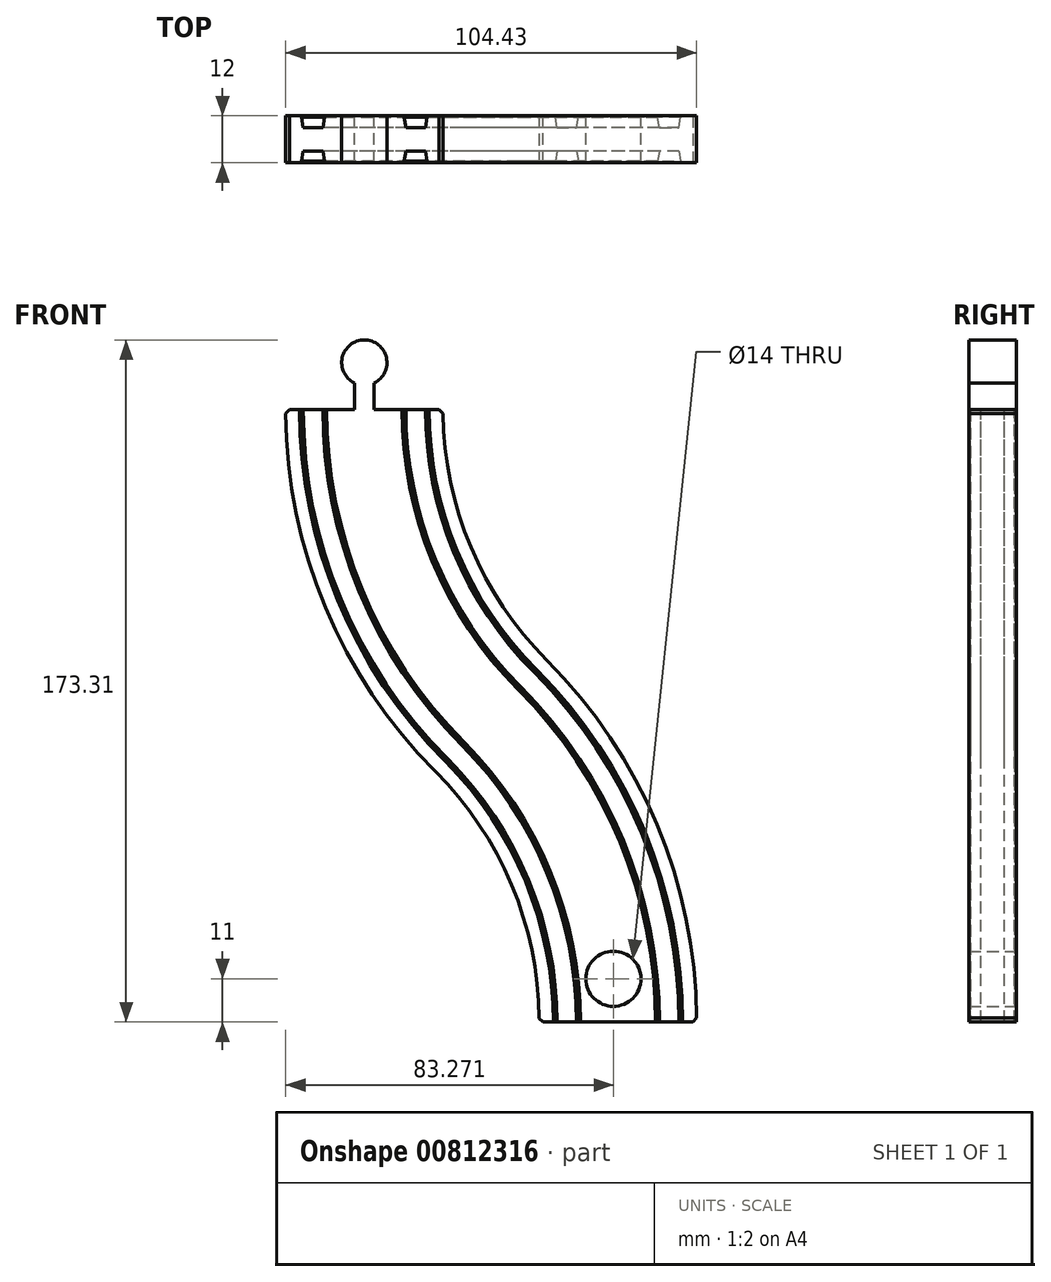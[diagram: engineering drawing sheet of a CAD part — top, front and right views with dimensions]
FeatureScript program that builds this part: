
annotation { "Feature Type Name" : "Feature", "Feature Type Description" : "" }
export const myFeature = defineFeature(function(context is Context, id is Id, definition is map)
    precondition{}
    {
        {
            var Q0;
            Q0=qCreatedBy(makeId("Top.planeOp"),FACE);
            var sketch = newSketch(context, id + "F0", { "sketchPlane" : qUnion([Q0])});
            skLineSegment(sketch, "E0.bottom", {"start": v(-20, 6) * mm, "end": v(20, 6) * mm});
            skLineSegment(sketch, "E0.top", {"start": v(-20, -6) * mm, "end": v(20, -6) * mm});
            skLineSegment(sketch, "E0.left", {"start": v(-20, 6) * mm, "end": v(-20, -6) * mm});
            skLineSegment(sketch, "E0.right", {"start": v(20, 6) * mm, "end": v(20, -6) * mm});
            skLineSegment(sketch, "E1", {"start": v(10.53, 3) * mm, "end": v(15.53, 3) * mm});
            skLineSegment(sketch, "E2", {"start": v(-15.53, 3) * mm, "end": v(-10.53, 3) * mm});
            skLineSegment(sketch, "E3", {"start": v(-20, 6) * mm, "end": v(20, -6) * mm, "construction": true});
            skLineSegment(sketch, "E4", {"start": v(-10.53, 3) * mm, "end": v(-10, 6) * mm});
            skLineSegment(sketch, "E5", {"start": v(-15.53, 3) * mm, "end": v(-16, 6) * mm});
            skLineSegment(sketch, "E6", {"start": v(10.53, 3) * mm, "end": v(10, 6) * mm});
            skLineSegment(sketch, "E7", {"start": v(15.53, 3) * mm, "end": v(16, 6) * mm});
            skLineSegment(sketch, "E8", {"start": v(15.53, -3) * mm, "end": v(10.53, -3) * mm});
            skLineSegment(sketch, "E9", {"start": v(15.53, -3) * mm, "end": v(16, -6) * mm});
            skLineSegment(sketch, "E10", {"start": v(10.53, -3) * mm, "end": v(10, -6) * mm});
            skLineSegment(sketch, "E11", {"start": v(-10.53, -3) * mm, "end": v(-15.53, -3) * mm});
            skLineSegment(sketch, "E12", {"start": v(-10.53, -3) * mm, "end": v(-10, -6) * mm});
            skLineSegment(sketch, "E13", {"start": v(-15.53, -3) * mm, "end": v(-16, -6) * mm});
            skLineSegment(sketch, "E14", {"start": v(10, 6) * mm, "end": v(10, -6) * mm, "construction": true});
            skLineSegment(sketch, "E15", {"start": v(16, 6) * mm, "end": v(16, -6) * mm, "construction": true});
            skLineSegment(sketch, "E16", {"start": v(10.53, 3) * mm, "end": v(10.53, -6) * mm, "construction": true});
            skLineSegment(sketch, "E17", {"start": v(-15.53, 3) * mm, "end": v(-15.53, -6) * mm, "construction": true});
            skSolve(sketch);
        }
        {
            var Q0;
            Q0=qCreatedBy(makeId("Front.planeOp"),FACE);
            var sketch = newSketch(context, id + "F1", { "sketchPlane" : qUnion([Q0])});
            skArc(sketch, "E18", {"start": v(0, 0) * mm, "mid": v(-8.37, 42.1) * mm, "end": v(-32.22, 77.78) * mm});
            skLineSegment(sketch, "E19", {"start": v(-110, 0) * mm, "end": v(45.56, 155.56) * mm, "construction": true});
            skArc(sketch, "E20", {"start": v(-32.22, 77.78) * mm, "mid": v(-56.06, 113.47) * mm, "end": v(-64.44, 155.56) * mm});
            skSolve(sketch);
        }
        {
            var Q0;
            Q0=makeQuery(id+"F0.imprint","IMPRINT",FACE,{"disambiguationData":[TD([[makeQuery(id+"F0.imprint","IMPRINT",EDGE,{"derivedFrom":sQuery(id+"F0.wireOp",EDGE,"E0.top")}),1.0]])]});
            var Q1;
            Q1=sQuery(id+"F1.wireOp",EDGE,"E18");
            var Q2;
            Q2=sQuery(id+"F1.wireOp",EDGE,"E20");
            sweep(context, id + "F2", {"profiles" : qUnion([Q0]), "path" : qUnion([Q1, Q2])});
        }
        {
            var Q0;
            Q0=makeQuery(id+"F2.opSweep","SWEPT_EDGE",EDGE,{"disambiguationData":[OSD([sQuery(id+"F0.wireOp",EDGE,"E0.bottom"),sQuery(id+"F0.wireOp",EDGE,"E4"),sQuery(id+"F1.wireOp",EDGE,"QheDVgyy-v1Xf-DTUT-CkoZ-R19I37jAeaWV")])]});
            var Q1;
            Q1=makeQuery(id+"F2.opSweep","SWEPT_EDGE",EDGE,{"disambiguationData":[OSD([sQuery(id+"F0.wireOp",EDGE,"E0.bottom"),sQuery(id+"F0.wireOp",EDGE,"E5"),sQuery(id+"F1.wireOp",EDGE,"QheDVgyy-v1Xf-DTUT-CkoZ-R19I37jAeaWV")])]});
            var Q2;
            Q2=makeQuery(id+"F2.opSweep","SWEPT_EDGE",EDGE,{"disambiguationData":[OSD([sQuery(id+"F0.wireOp",EDGE,"E0.bottom"),sQuery(id+"F0.wireOp",EDGE,"E6"),sQuery(id+"F1.wireOp",EDGE,"QheDVgyy-v1Xf-DTUT-CkoZ-R19I37jAeaWV")])]});
            var Q3;
            Q3=makeQuery(id+"F2.opSweep","SWEPT_EDGE",EDGE,{"disambiguationData":[OSD([sQuery(id+"F0.wireOp",EDGE,"E0.bottom"),sQuery(id+"F0.wireOp",EDGE,"E7"),sQuery(id+"F1.wireOp",EDGE,"QheDVgyy-v1Xf-DTUT-CkoZ-R19I37jAeaWV")])]});
            var Q4;
            Q4=makeQuery(id+"F2.opSweep","SWEPT_EDGE",EDGE,{"disambiguationData":[OSD([sQuery(id+"F0.wireOp",EDGE,"E0.top"),sQuery(id+"F0.wireOp",EDGE,"E10"),sQuery(id+"F1.wireOp",EDGE,"E18")])]});
            var Q5;
            Q5=makeQuery(id+"F2.opSweep","SWEPT_EDGE",EDGE,{"disambiguationData":[OSD([sQuery(id+"F0.wireOp",EDGE,"E0.top"),sQuery(id+"F0.wireOp",EDGE,"E9"),sQuery(id+"F1.wireOp",EDGE,"E18")])]});
            var Q6;
            Q6=makeQuery(id+"F2.opSweep","SWEPT_EDGE",EDGE,{"disambiguationData":[OSD([sQuery(id+"F0.wireOp",EDGE,"E0.top"),sQuery(id+"F0.wireOp",EDGE,"E13"),sQuery(id+"F1.wireOp",EDGE,"E18")])]});
            var Q7;
            Q7=makeQuery(id+"F2.opSweep","SWEPT_EDGE",EDGE,{"disambiguationData":[OSD([sQuery(id+"F0.wireOp",EDGE,"E0.top"),sQuery(id+"F0.wireOp",EDGE,"E12"),sQuery(id+"F1.wireOp",EDGE,"E18")])]});
            chamfer(context, id + "F3", {"entities" : qUnion([Q0, Q1, Q2, Q3, Q4, Q5, Q6, Q7]), "width" : 0.5 * mm, "tangentPropagation" : true});
        }
        {
            var Q0;
            Q0=qCreatedBy(makeId("Front.planeOp"),FACE);
            var sketch = newSketch(context, id + "F4", { "sketchPlane" : qUnion([Q0])});
            skLineSegment(sketch, "E21.0", {"start": v(-47.4, 155.56) * mm, "end": v(-54.94, 155.56) * mm});
            skSolve(sketch);
        }
        {
            var Q0;
            Q0=qCreatedBy(makeId("Front.planeOp"),FACE);
            var sketch = newSketch(context, id + "F5", { "sketchPlane" : qUnion([Q0])});
            skLineSegment(sketch, "E22.0", {"start": v(-9.5, 0) * mm, "end": v(-9.5, 0) * mm});
            skLineSegment(sketch, "E23.bottom", {"start": v(2.34, 0) * mm, "end": v(-4.66, 0) * mm});
            skLineSegment(sketch, "E23.top", {"start": v(2.34, 5) * mm, "end": v(-4.66, 5) * mm});
            skLineSegment(sketch, "E23.left", {"start": v(2.34, 0) * mm, "end": v(2.34, 5) * mm});
            skLineSegment(sketch, "E23.right", {"start": v(-4.66, 0) * mm, "end": v(-4.66, 5) * mm});
            skLineSegment(sketch, "E24", {"start": v(8.34, 0) * mm, "end": v(2.34, 0) * mm, "construction": true});
            skLineSegment(sketch, "E25", {"start": v(-4.66, 0) * mm, "end": v(-10.66, 0) * mm, "construction": true});
            skCircle(sketch, "E26", {"center": v(-1.16, 11) * mm, "radius": 7 * mm});
            skPoint(sketch, "E26.centerSnap0", {"position": v(-1.16, 5) * mm});
            skSolve(sketch);
        }
        {
            var Q0;
            {var subQ0=sQuery(id+"F1.wireOp",EDGE,"QheDVgyy-v1Xf-DTUT-CkoZ-R19I37jAeaWV");var subQ1=sQuery(id+"F0.wireOp",EDGE,"E0.bottom");Q0=makeQuery(id+"F2.opSweep","SWEPT_FACE",FACE,{"disambiguationData":[OSD([subQ1,subQ0]),TDD([makeQuery(id+"F0.imprint","IMPRINT",EDGE,{"disambiguationData":[TD([[makeQuery(id+"F0.imprint","INTERSECT",VERTEX,{"derivedFrom":[subQ1,sQuery(id+"F0.wireOp",EDGE,"E4")]}),-1.0]])],"derivedFrom":subQ1}),subQ0])]});}
            var sketch = newSketch(context, id + "F6", { "sketchPlane" : qUnion([Q0])});
            skCircle(sketch, "E27.0", {"center": v(1.16, 11) * mm, "radius": 7 * mm});
            skLineSegment(sketch, "E28.0", {"start": v(4.66, 0) * mm, "end": v(4.66, 5) * mm});
            skLineSegment(sketch, "E29.0", {"start": v(-2.34, 0) * mm, "end": v(-2.34, 5) * mm});
            skLineSegment(sketch, "E30.0", {"start": v(-2.34, 5) * mm, "end": v(4.66, 5) * mm});
            skLineSegment(sketch, "E31.0", {"start": v(-8.34, 0) * mm, "end": v(10.66, 0) * mm});
            skSolve(sketch);
        }
        {
            var Q0;
            {var subQ5=sQuery(id+"F6.wireOp",EDGE,"E30.0");Q0=makeQuery(id+"F6.imprint","IMPRINT",FACE,{"disambiguationData":[TD([[makeQuery(id+"F6.imprint","IMPRINT",EDGE,{"derivedFrom":subQ5}),1.0]])]});}
            var Q1;
            {var subQ0=sQuery(id+"F6.wireOp",EDGE,"E28.0");var subQ1=sQuery(id+"F6.wireOp",EDGE,"E27.0");var subQ2=makeQuery(id+"F6.imprint","INTERSECT",VERTEX,{"derivedFrom":[subQ1,subQ0]});Q1=makeQuery(id+"F6.imprint","IMPRINT",FACE,{"disambiguationData":[TD([[makeQuery(id+"F6.imprint","IMPRINT",EDGE,{"disambiguationData":[TD([[subQ2,-1.0]])],"derivedFrom":subQ1}),1.0]])]});}
            var Q2;
            {var subQ5=sQuery(id+"F6.wireOp",EDGE,"E30.0");Q2=makeQuery(id+"F6.imprint","IMPRINT",FACE,{"disambiguationData":[TD([[makeQuery(id+"F6.imprint","IMPRINT",EDGE,{"derivedFrom":subQ5}),-1.0]])]});}
            extrude(context, id + "F7", {"entities" : qUnion([Q0, Q1, Q2]), "operationType" : NewBodyOperationType.REMOVE, "oppositeDirection" : true, "depth" : 25.4 * mm, "offsetDistance" : 25.4 * mm});
        }
        {
            var Q0;
            Q0=makeQuery(id+"F2.opSweep","CAP_EDGE",EDGE,{"disambiguationData":[OSD([sQuery(id+"F0.wireOp",EDGE,"E0.right"),sQuery(id+"F1.wireOp",VERTEX,"QheDVgyy-v1Xf-DTUT-CkoZ-R19I37jAeaWV.start")])],"isStart":false});
            var Q1;
            Q1=makeQuery(id+"F2.opSweep","CAP_EDGE",EDGE,{"disambiguationData":[OSD([sQuery(id+"F0.wireOp",EDGE,"E0.left"),sQuery(id+"F1.wireOp",VERTEX,"QheDVgyy-v1Xf-DTUT-CkoZ-R19I37jAeaWV.start")])],"isStart":false});
            var Q2;
            Q2=makeQuery(id+"F2.opSweep","CAP_EDGE",EDGE,{"disambiguationData":[OSD([sQuery(id+"F0.wireOp",EDGE,"E0.left"),sQuery(id+"F1.wireOp",VERTEX,"QheDVgyy-v1Xf-DTUT-CkoZ-R19I37jAeaWV.end")])],"isStart":true});
            var Q3;
            Q3=makeQuery(id+"F2.opSweep","CAP_EDGE",EDGE,{"disambiguationData":[OSD([sQuery(id+"F0.wireOp",EDGE,"E0.right"),sQuery(id+"F1.wireOp",VERTEX,"QheDVgyy-v1Xf-DTUT-CkoZ-R19I37jAeaWV.end")])],"isStart":true});
            chamfer(context, id + "F8", {"entities" : qUnion([Q0, Q1, Q2, Q3]), "width" : 1 * mm, "tangentPropagation" : true});
        }
        {
            var Q0;
            {var subQ0=sQuery(id+"F1.wireOp",EDGE,"E18");var subQ1=sQuery(id+"F0.wireOp",EDGE,"E0.bottom");Q0=makeQuery(id+"F2.opSweep","SWEPT_FACE",FACE,{"disambiguationData":[OSD([subQ1,subQ0]),TDD([makeQuery(id+"F0.imprint","IMPRINT",EDGE,{"disambiguationData":[TD([[makeQuery(id+"F0.imprint","INTERSECT",VERTEX,{"derivedFrom":[subQ1,sQuery(id+"F0.wireOp",EDGE,"E4")]}),-1.0]])],"derivedFrom":subQ1}),subQ0])]});}
            var sketch = newSketch(context, id + "F9", { "sketchPlane" : qUnion([Q0])});
            skLineSegment(sketch, "E32", {"start": v(61.94, 155.56) * mm, "end": v(61.94, 162.56) * mm});
            skLineSegment(sketch, "E33", {"start": v(61.94, 162.56) * mm, "end": v(66.94, 162.56) * mm});
            skLineSegment(sketch, "E34", {"start": v(66.94, 162.56) * mm, "end": v(66.94, 155.56) * mm});
            skLineSegment(sketch, "E35", {"start": v(61.94, 155.56) * mm, "end": v(54.94, 155.56) * mm, "construction": true});
            skLineSegment(sketch, "E36", {"start": v(66.94, 155.56) * mm, "end": v(73.94, 155.56) * mm, "construction": true});
            skLineSegment(sketch, "E37", {"start": v(64.44, 155.56) * mm, "end": v(64.44, 167.56) * mm, "construction": true});
            skCircle(sketch, "E38", {"center": v(64.44, 167.56) * mm, "radius": 5.75 * mm});
            skSolve(sketch);
        }
        {
            var Q0;
            {var subQ0=sQuery(id+"F4.wireOp",EDGE,"y3DwgqY9-x9Yp-s0zT-CjDQ-IHoX7M89SHfb");var subQ1=sQuery(id+"F4.wireOp",EDGE,"XYbCKtlu-qh1t-nVi3-P5wv-khNMWSoX9qSB");var subQ2=makeQuery(id+"F4.imprint","INTERSECT",VERTEX,{"derivedFrom":[subQ1,subQ0]});Q0=makeQuery(id+"F4.imprint","IMPRINT",FACE,{"disambiguationData":[TD([[makeQuery(id+"F4.imprint","IMPRINT",EDGE,{"disambiguationData":[TD([[subQ2,1.0]])],"derivedFrom":subQ1}),-1.0]])]});}
            var Q1;
            {var subQ0=sQuery(id+"F4.wireOp",EDGE,"rqF1hGhq-thtG-Dqzb-XRaq-cd5KwwhKuCuG");var subQ1=sQuery(id+"F4.wireOp",EDGE,"E21.0");var subQ2=makeQuery(id+"F4.imprint","INTERSECT",VERTEX,{"derivedFrom":[subQ1,subQ0]});Q1=makeQuery(id+"F4.imprint","IMPRINT",FACE,{"disambiguationData":[TD([[makeQuery(id+"F4.imprint","IMPRINT",EDGE,{"disambiguationData":[TD([[subQ2,-1.0]])],"derivedFrom":subQ1}),-1.0]])]});}
            var Q2;
            {var subQ0=sQuery(id+"F4.wireOp",EDGE,"y3DwgqY9-x9Yp-s0zT-CjDQ-IHoX7M89SHfb");var subQ1=sQuery(id+"F4.wireOp",EDGE,"E21.0");var subQ2=makeQuery(id+"F4.imprint","INTERSECT",VERTEX,{"derivedFrom":[subQ1,subQ0]});Q2=makeQuery(id+"F4.imprint","IMPRINT",FACE,{"disambiguationData":[TD([[makeQuery(id+"F4.imprint","IMPRINT",EDGE,{"disambiguationData":[TD([[subQ2,1.0]])],"derivedFrom":subQ1}),-1.0]])]});}
            var Q3;
            {var subQ0=sQuery(id+"F4.wireOp",EDGE,"y3DwgqY9-x9Yp-s0zT-CjDQ-IHoX7M89SHfb");var subQ1=sQuery(id+"F4.wireOp",EDGE,"XYbCKtlu-qh1t-nVi3-P5wv-khNMWSoX9qSB");var subQ2=makeQuery(id+"F4.imprint","INTERSECT",VERTEX,{"derivedFrom":[subQ1,subQ0]});Q3=makeQuery(id+"F4.imprint","IMPRINT",FACE,{"disambiguationData":[TD([[makeQuery(id+"F4.imprint","IMPRINT",EDGE,{"disambiguationData":[TD([[subQ2,1.0]])],"derivedFrom":subQ1}),1.0]])]});}
            var Q4;
            {var subQ0=sQuery(id+"F4.wireOp",EDGE,"XYbCKtlu-qh1t-nVi3-P5wv-khNMWSoX9qSB");var subQ1=sQuery(id+"F4.wireOp",EDGE,"rqF1hGhq-thtG-Dqzb-XRaq-cd5KwwhKuCuG");var subQ2=makeQuery(id+"F4.imprint","INTERSECT",VERTEX,{"derivedFrom":[subQ1,subQ0]});Q4=makeQuery(id+"F4.imprint","IMPRINT",FACE,{"disambiguationData":[TD([[makeQuery(id+"F4.imprint","IMPRINT",EDGE,{"disambiguationData":[TD([[subQ2,1.0]])],"derivedFrom":subQ1}),-1.0]])]});}
            var Q5;
            {var subQ0=sQuery(id+"F4.wireOp",EDGE,"XYbCKtlu-qh1t-nVi3-P5wv-khNMWSoX9qSB");var subQ1=sQuery(id+"F4.wireOp",EDGE,"rqF1hGhq-thtG-Dqzb-XRaq-cd5KwwhKuCuG");var subQ2=makeQuery(id+"F4.imprint","INTERSECT",VERTEX,{"derivedFrom":[subQ1,subQ0]});Q5=makeQuery(id+"F4.imprint","IMPRINT",FACE,{"disambiguationData":[TD([[makeQuery(id+"F4.imprint","IMPRINT",EDGE,{"disambiguationData":[TD([[subQ2,1.0]])],"derivedFrom":subQ1}),1.0]])]});}
            var Q6;
            {var subQ0=sQuery(id+"F9.wireOp",EDGE,"E32");Q6=makeQuery(id+"F9.imprint","IMPRINT",FACE,{"disambiguationData":[TD([[makeQuery(id+"F9.imprint","IMPRINT",EDGE,{"derivedFrom":subQ0}),-1.0]])]});}
            var Q7;
            {var subQ0=sQuery(id+"F9.wireOp",EDGE,"E38");var subQ1=sQuery(id+"F9.wireOp",EDGE,"E33");var subQ2=makeQuery(id+"F9.imprint","INTERSECT",VERTEX,{"disambiguationData":[OD(0.0)],"derivedFrom":[subQ1,subQ0]});Q7=makeQuery(id+"F9.imprint","IMPRINT",FACE,{"disambiguationData":[TD([[makeQuery(id+"F9.imprint","IMPRINT",EDGE,{"disambiguationData":[TD([[subQ2,-1.0]])],"derivedFrom":subQ1}),1.0]])]});}
            var Q8;
            {var subQ0=sQuery(id+"F9.wireOp",EDGE,"E38");var subQ1=sQuery(id+"F9.wireOp",EDGE,"E33");var subQ2=makeQuery(id+"F9.imprint","INTERSECT",VERTEX,{"disambiguationData":[OD(0.0)],"derivedFrom":[subQ1,subQ0]});Q8=makeQuery(id+"F9.imprint","IMPRINT",FACE,{"disambiguationData":[TD([[makeQuery(id+"F9.imprint","IMPRINT",EDGE,{"disambiguationData":[TD([[subQ2,-1.0]])],"derivedFrom":subQ1}),-1.0]])]});}
            extrude(context, id + "F10", {"entities" : qUnion([Q0, Q1, Q2, Q3, Q4, Q5, Q6, Q7, Q8]), "operationType" : NewBodyOperationType.ADD, "oppositeDirection" : true, "depth" : 12 * mm, "offsetDistance" : 25.4 * mm});
        }
    });
